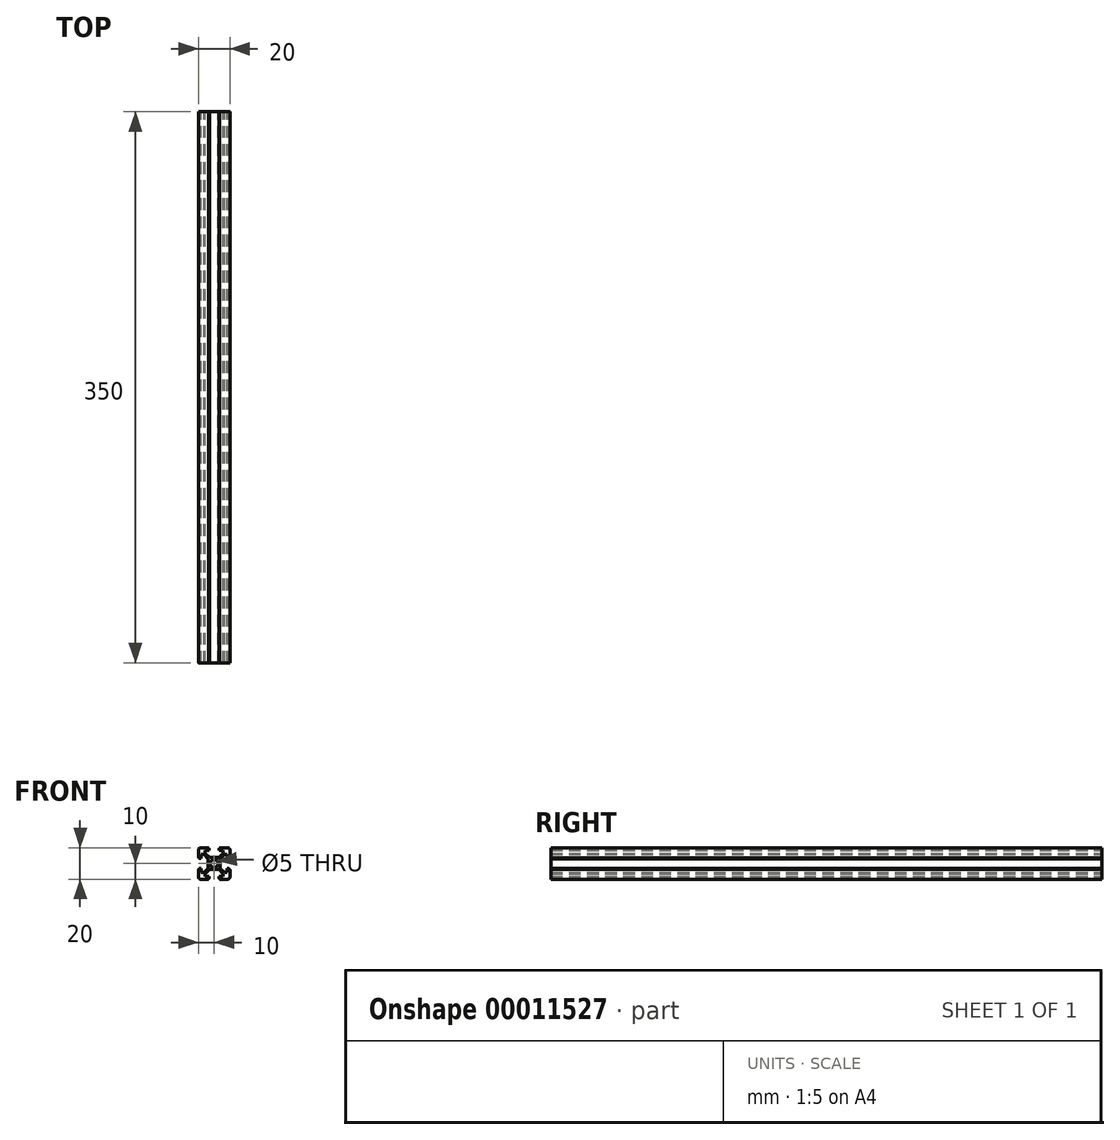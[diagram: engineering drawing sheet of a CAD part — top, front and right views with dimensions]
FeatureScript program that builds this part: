
annotation { "Feature Type Name" : "Feature", "Feature Type Description" : "" }
export const myFeature = defineFeature(function(context is Context, id is Id, definition is map)
    precondition{}
    {
        {
            var Q0;
            Q0=qCreatedBy(makeId("Front.planeOp"),FACE);
            var sketch = newSketch(context, id + "F0", { "sketchPlane" : qUnion([Q0])});
            skLineSegment(sketch, "E0", {"start": v(-10, 8.5) * mm, "end": v(-10, 3.6) * mm});
            skLineSegment(sketch, "E1", {"start": v(-10, 3.6) * mm, "end": v(-9.5, 3.6) * mm});
            skLineSegment(sketch, "E2", {"start": v(-9.5, 3.6) * mm, "end": v(-9.5, 3.1) * mm});
            skLineSegment(sketch, "E3", {"start": v(-9.5, 3.1) * mm, "end": v(-8.3, 3.1) * mm});
            skLineSegment(sketch, "E4", {"start": v(-8.3, 3.1) * mm, "end": v(-8.3, 5.63) * mm});
            skLineSegment(sketch, "E5", {"start": v(-8.3, 5.63) * mm, "end": v(-6.53, 5.63) * mm});
            skLineSegment(sketch, "E6", {"start": v(-6.53, 5.63) * mm, "end": v(-3.9, 3) * mm});
            skLineSegment(sketch, "E7", {"start": v(-8.5, 10) * mm, "end": v(-3.6, 10) * mm});
            skLineSegment(sketch, "E8", {"start": v(-3.6, 10) * mm, "end": v(-3.6, 9.5) * mm});
            skLineSegment(sketch, "E9", {"start": v(-3.6, 9.5) * mm, "end": v(-3.1, 9.5) * mm});
            skLineSegment(sketch, "E10", {"start": v(-3.1, 9.5) * mm, "end": v(-3.1, 8.3) * mm});
            skLineSegment(sketch, "E11", {"start": v(-3.1, 8.3) * mm, "end": v(-5.63, 8.3) * mm});
            skLineSegment(sketch, "E12", {"start": v(-5.63, 8.3) * mm, "end": v(-5.63, 6.53) * mm});
            skLineSegment(sketch, "E13", {"start": v(-5.63, 6.53) * mm, "end": v(-3, 3.9) * mm});
            skPoint(sketch, "E14.visualSharp", {"position": v(-10, 10) * mm});
            skArc(sketch, "E14.filletArc", {"start": v(-8.5, 10) * mm, "mid": v(-9.56, 9.56) * mm, "end": v(-10, 8.5) * mm});
            skLineSegment(sketch, "E15.0.MirrorCS", {"start": v(3.1, 9.5) * mm, "end": v(3.1, 8.3) * mm});
            skLineSegment(sketch, "E15.1.MirrorCS", {"start": v(3.6, 9.5) * mm, "end": v(3.1, 9.5) * mm});
            skLineSegment(sketch, "E15.2.MirrorCS", {"start": v(3.6, 10) * mm, "end": v(3.6, 9.5) * mm});
            skLineSegment(sketch, "E15.3.MirrorCS", {"start": v(3.1, 8.3) * mm, "end": v(5.63, 8.3) * mm});
            skLineSegment(sketch, "E15.4.MirrorCS", {"start": v(9.5, 3.6) * mm, "end": v(9.5, 3.1) * mm});
            skLineSegment(sketch, "E15.5.MirrorCS", {"start": v(10, 3.6) * mm, "end": v(9.5, 3.6) * mm});
            skLineSegment(sketch, "E15.6.MirrorCS", {"start": v(8.3, 3.1) * mm, "end": v(8.3, 5.63) * mm});
            skArc(sketch, "E15.7.MirrorCS", {"start": v(8.5, 10) * mm, "mid": v(9.56, 9.56) * mm, "end": v(10, 8.5) * mm});
            skLineSegment(sketch, "E15.8.MirrorCS", {"start": v(9.5, 3.1) * mm, "end": v(8.3, 3.1) * mm});
            skLineSegment(sketch, "E15.9.MirrorCS", {"start": v(5.63, 8.3) * mm, "end": v(5.63, 6.53) * mm});
            skLineSegment(sketch, "E15.10.MirrorCS", {"start": v(8.3, 5.63) * mm, "end": v(6.53, 5.63) * mm});
            skLineSegment(sketch, "E15.12.MirrorCS", {"start": v(8.5, 10) * mm, "end": v(3.6, 10) * mm});
            skLineSegment(sketch, "E15.13.MirrorCS", {"start": v(6.53, 5.63) * mm, "end": v(3.9, 3) * mm});
            skPoint(sketch, "E15.14.MirrorP", {"position": v(10, 10) * mm});
            skLineSegment(sketch, "E15.15.MirrorCS", {"start": v(10, 8.5) * mm, "end": v(10, 3.6) * mm});
            skLineSegment(sketch, "E15.17.MirrorCS", {"start": v(5.63, 6.53) * mm, "end": v(3, 3.9) * mm});
            skLineSegment(sketch, "E16.0.MirrorCS", {"start": v(-5.63, -8.3) * mm, "end": v(-5.63, -6.53) * mm});
            skLineSegment(sketch, "E16.1.MirrorCS", {"start": v(-3.1, -9.5) * mm, "end": v(-3.1, -8.3) * mm});
            skLineSegment(sketch, "E16.2.MirrorCS", {"start": v(-3.1, -8.3) * mm, "end": v(-5.63, -8.3) * mm});
            skLineSegment(sketch, "E16.3.MirrorCS", {"start": v(-10, -3.6) * mm, "end": v(-9.5, -3.6) * mm});
            skLineSegment(sketch, "E16.4.MirrorCS", {"start": v(-3.6, -10) * mm, "end": v(-3.6, -9.5) * mm});
            skLineSegment(sketch, "E16.5.MirrorCS", {"start": v(8.3, -3.1) * mm, "end": v(8.3, -5.63) * mm});
            skLineSegment(sketch, "E16.6.MirrorCS", {"start": v(8.3, -5.63) * mm, "end": v(6.53, -5.63) * mm});
            skLineSegment(sketch, "E16.7.MirrorCS", {"start": v(3.1, -9.5) * mm, "end": v(3.1, -8.3) * mm});
            skLineSegment(sketch, "E16.8.MirrorCS", {"start": v(10, -3.6) * mm, "end": v(9.5, -3.6) * mm});
            skLineSegment(sketch, "E16.9.MirrorCS", {"start": v(9.5, -3.1) * mm, "end": v(8.3, -3.1) * mm});
            skLineSegment(sketch, "E16.10.MirrorCS", {"start": v(-10, -8.5) * mm, "end": v(-10, -3.6) * mm});
            skLineSegment(sketch, "E16.11.MirrorCS", {"start": v(-5.63, -6.53) * mm, "end": v(-3, -3.9) * mm});
            skLineSegment(sketch, "E16.12.MirrorCS", {"start": v(3.1, -8.3) * mm, "end": v(5.63, -8.3) * mm});
            skLineSegment(sketch, "E16.14.MirrorCS", {"start": v(10, -8.5) * mm, "end": v(10, -3.6) * mm});
            skLineSegment(sketch, "E16.15.MirrorCS", {"start": v(3.6, -10) * mm, "end": v(3.6, -9.5) * mm});
            skLineSegment(sketch, "E16.17.MirrorCS", {"start": v(8.5, -10) * mm, "end": v(3.6, -10) * mm});
            skLineSegment(sketch, "E16.18.MirrorCS", {"start": v(5.63, -8.3) * mm, "end": v(5.63, -6.53) * mm});
            skArc(sketch, "E16.20.MirrorCS", {"start": v(-8.5, -10) * mm, "mid": v(-9.56, -9.56) * mm, "end": v(-10, -8.5) * mm});
            skLineSegment(sketch, "E16.21.MirrorCS", {"start": v(6.53, -5.63) * mm, "end": v(3.9, -3) * mm});
            skLineSegment(sketch, "E16.22.MirrorCS", {"start": v(5.63, -6.53) * mm, "end": v(3, -3.9) * mm});
            skLineSegment(sketch, "E16.23.MirrorCS", {"start": v(-6.53, -5.63) * mm, "end": v(-3.9, -3) * mm});
            skLineSegment(sketch, "E16.25.MirrorCS", {"start": v(-8.5, -10) * mm, "end": v(-3.6, -10) * mm});
            skLineSegment(sketch, "E16.26.MirrorCS", {"start": v(-8.3, -5.63) * mm, "end": v(-6.53, -5.63) * mm});
            skLineSegment(sketch, "E16.27.MirrorCS", {"start": v(-8.3, -3.1) * mm, "end": v(-8.3, -5.63) * mm});
            skLineSegment(sketch, "E16.28.MirrorCS", {"start": v(-9.5, -3.1) * mm, "end": v(-8.3, -3.1) * mm});
            skArc(sketch, "E16.29.MirrorCS", {"start": v(8.5, -10) * mm, "mid": v(9.56, -9.56) * mm, "end": v(10, -8.5) * mm});
            skPoint(sketch, "E16.30.MirrorP", {"position": v(10, -10) * mm});
            skPoint(sketch, "E16.31.MirrorP", {"position": v(-10, -10) * mm});
            skCircle(sketch, "E17", {"center": v(0, 0) * mm, "radius": 2.5 * mm});
            skLineSegment(sketch, "E18", {"start": v(-9.5, -3.6) * mm, "end": v(-9.5, -3.1) * mm});
            skLineSegment(sketch, "E19", {"start": v(-3.1, -9.5) * mm, "end": v(-3.6, -9.5) * mm});
            skLineSegment(sketch, "E20", {"start": v(3.1, -9.5) * mm, "end": v(3.6, -9.5) * mm});
            skLineSegment(sketch, "E21", {"start": v(9.5, -3.6) * mm, "end": v(9.5, -3.1) * mm});
            skLineSegment(sketch, "E22", {"start": v(-3, 3.9) * mm, "end": v(3, 3.9) * mm});
            skLineSegment(sketch, "E23", {"start": v(3.9, 3) * mm, "end": v(3.9, -3) * mm});
            skLineSegment(sketch, "E24", {"start": v(3, -3.9) * mm, "end": v(-3, -3.9) * mm});
            skLineSegment(sketch, "E25", {"start": v(-3.9, -3) * mm, "end": v(-3.9, 3) * mm});
            skSolve(sketch);
        }
        {
            var Q0;
            Q0=makeQuery(id+"F0.imprint","IMPRINT",FACE,{"disambiguationData":[TD([[makeQuery(id+"F0.imprint","IMPRINT",EDGE,{"derivedFrom":sQuery(id+"F0.wireOp",EDGE,"E0")}),1.0]])]});
            extrude(context, id + "F1", {"entities" : qUnion([Q0]), "endBound" : BoundingType.SYMMETRIC, "depth" : 350 * mm});
        }
    });
